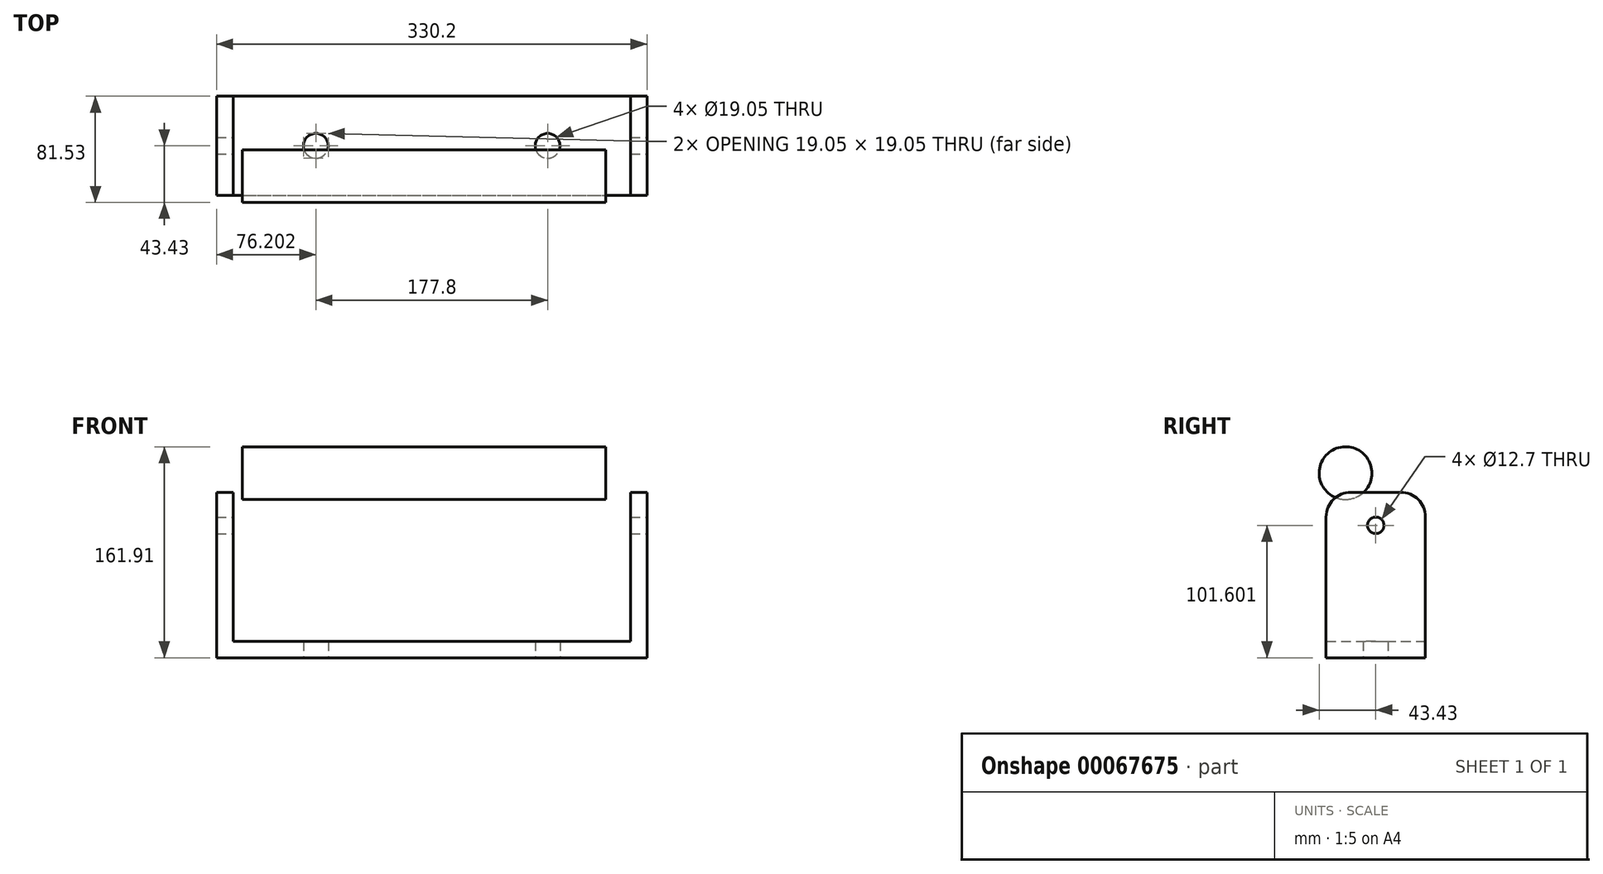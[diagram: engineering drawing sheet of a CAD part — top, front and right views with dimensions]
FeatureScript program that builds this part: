
annotation { "Feature Type Name" : "Feature", "Feature Type Description" : "" }
export const myFeature = defineFeature(function(context is Context, id is Id, definition is map)
    precondition{}
    {
        {
            var Q0;
            Q0=qCreatedBy(makeId("Front.planeOp"),FACE);
            var sketch = newSketch(context, id + "F0", { "sketchPlane" : qUnion([Q0])});
            skLineSegment(sketch, "E0.bottom", {"start": v(-115.73, 44.46) * mm, "end": v(-103.03, 44.46) * mm});
            skLineSegment(sketch, "E0.top", {"start": v(-115.73, -82.54) * mm, "end": v(214.47, -82.54) * mm});
            skLineSegment(sketch, "E0.left", {"start": v(-115.73, 44.46) * mm, "end": v(-115.73, -82.54) * mm});
            skLineSegment(sketch, "E0.right", {"start": v(214.47, 44.46) * mm, "end": v(214.47, -82.54) * mm});
            skLineSegment(sketch, "E1.top", {"start": v(-103.03, -69.84) * mm, "end": v(201.77, -69.84) * mm});
            skLineSegment(sketch, "E1.left", {"start": v(-103.03, 44.46) * mm, "end": v(-103.03, -69.84) * mm});
            skLineSegment(sketch, "E1.right", {"start": v(201.77, 44.46) * mm, "end": v(201.77, -69.84) * mm});
            skLineSegment(sketch, "E2.trimOffspring", {"start": v(201.77, 44.46) * mm, "end": v(214.47, 44.46) * mm});
            skSolve(sketch);
        }
        {
            var Q0;
            Q0=makeQuery(id+"F0.imprint","IMPRINT",FACE,{"disambiguationData":[TD([[makeQuery(id+"F0.imprint","IMPRINT",EDGE,{"derivedFrom":sQuery(id+"F0.wireOp",EDGE,"E0.bottom")}),-1.0]])]});
            extrude(context, id + "F1", {"entities" : qUnion([Q0]), "depth" : 76.2 * mm});
        }
        {
            var Q0;
            Q0=makeQuery(id+"F1.opExtrude","SWEPT_FACE",FACE,{"disambiguationData":[OSD([sQuery(id+"F0.wireOp",EDGE,"E0.right")])]});
            var sketch = newSketch(context, id + "F2", { "sketchPlane" : qUnion([Q0])});
            skPoint(sketch, "E3", {"position": v(-38.1, 19.06) * mm});
            skSolve(sketch);
        }
        {
            var Q0;
            Q0=sQuery(id+"F2.wireOp",VERTEX,"E3");
            var Q1;
            Q1=makeQuery(id+"F1.opExtrude","SWEPT_BODY",BODY,{"disambiguationData":[OSD([sQuery(id+"F0.wireOp",EDGE,"E0.bottom"),sQuery(id+"F0.wireOp",EDGE,"E0.top"),sQuery(id+"F0.wireOp",EDGE,"E0.left"),sQuery(id+"F0.wireOp",EDGE,"E0.right"),sQuery(id+"F0.wireOp",EDGE,"E1.top"),sQuery(id+"F0.wireOp",EDGE,"E1.left"),sQuery(id+"F0.wireOp",EDGE,"E1.right"),sQuery(id+"F0.wireOp",EDGE,"E2.trimOffspring")])]});
            hole(context, id + "F3", {"style" : HoleStyle.SIMPLE, "holeDiameter" : 12.7 * mm, "endStyle" : HoleEndStyle.THROUGH, "locations" : qUnion([Q0]), "scope" : qUnion([Q1])});
        }
        {
            var Q0;
            Q0=makeQuery(id+"F1.opExtrude","CAP_EDGE",EDGE,{"disambiguationData":[OSD([sQuery(id+"F0.wireOp",EDGE,"E2.trimOffspring")])],"isStart":false});
            var Q1;
            Q1=makeQuery(id+"F1.opExtrude","CAP_EDGE",EDGE,{"disambiguationData":[OSD([sQuery(id+"F0.wireOp",EDGE,"E2.trimOffspring")])],"isStart":true});
            var Q2;
            Q2=makeQuery(id+"F1.opExtrude","CAP_EDGE",EDGE,{"disambiguationData":[OSD([sQuery(id+"F0.wireOp",EDGE,"E0.bottom")])],"isStart":false});
            var Q3;
            Q3=makeQuery(id+"F1.opExtrude","CAP_EDGE",EDGE,{"disambiguationData":[OSD([sQuery(id+"F0.wireOp",EDGE,"E0.bottom")])],"isStart":true});
            fillet(context, id + "F4", {"entities" : qUnion([Q0, Q1, Q2, Q3]), "radius" : 19.05 * mm, "tangentPropagation" : true, "allowEdgeOverflow" : false});
        }
        {
            var Q0;
            Q0=makeQuery(id+"F1.opExtrude","SWEPT_FACE",FACE,{"disambiguationData":[OSD([sQuery(id+"F0.wireOp",EDGE,"E0.top")])]});
            var sketch = newSketch(context, id + "F5", { "sketchPlane" : qUnion([Q0])});
            skPoint(sketch, "E4", {"position": v(-39.53, 38.1) * mm});
            skPoint(sketch, "E5", {"position": v(138.27, 38.1) * mm});
            skSolve(sketch);
        }
        {
            var Q0;
            Q0=sQuery(id+"F5.wireOp",VERTEX,"E4");
            var Q1;
            Q1=sQuery(id+"F5.wireOp",VERTEX,"E5");
            var Q2;
            Q2=makeQuery(id+"F1.opExtrude","SWEPT_BODY",BODY,{"disambiguationData":[OSD([sQuery(id+"F0.wireOp",EDGE,"E0.bottom"),sQuery(id+"F0.wireOp",EDGE,"E0.top"),sQuery(id+"F0.wireOp",EDGE,"E0.left"),sQuery(id+"F0.wireOp",EDGE,"E0.right"),sQuery(id+"F0.wireOp",EDGE,"E1.top"),sQuery(id+"F0.wireOp",EDGE,"E1.left"),sQuery(id+"F0.wireOp",EDGE,"E1.right"),sQuery(id+"F0.wireOp",EDGE,"E2.trimOffspring")])]});
            hole(context, id + "F6", {"style" : HoleStyle.SIMPLE, "holeDiameter" : 19.05 * mm, "endStyle" : HoleEndStyle.THROUGH, "locations" : qUnion([Q0, Q1]), "scope" : qUnion([Q2])});
        }
        {
            var Q0;
            Q0=qCreatedBy(makeId("Right.planeOp"),FACE);
            var sketch = newSketch(context, id + "F7", { "sketchPlane" : qUnion([Q0])});
            skCircle(sketch, "E6", {"center": v(-61.3, 59.14) * mm, "radius": 20.24 * mm});
            skSolve(sketch);
        }
        {
            var Q0;
            Q0=makeQuery(id+"F7.imprint","IMPRINT",FACE,{"disambiguationData":[TD([[makeQuery(id+"F7.imprint","IMPRINT",EDGE,{"derivedFrom":sQuery(id+"F7.wireOp",EDGE,"E6")}),1.0]])]});
            extrude(context, id + "F8", {"entities" : qUnion([Q0]), "depth" : 182.82 * mm, "hasSecondDirection" : true, "secondDirectionOppositeDirection" : true, "secondDirectionDepth" : 95.9 * mm});
        }
    });
